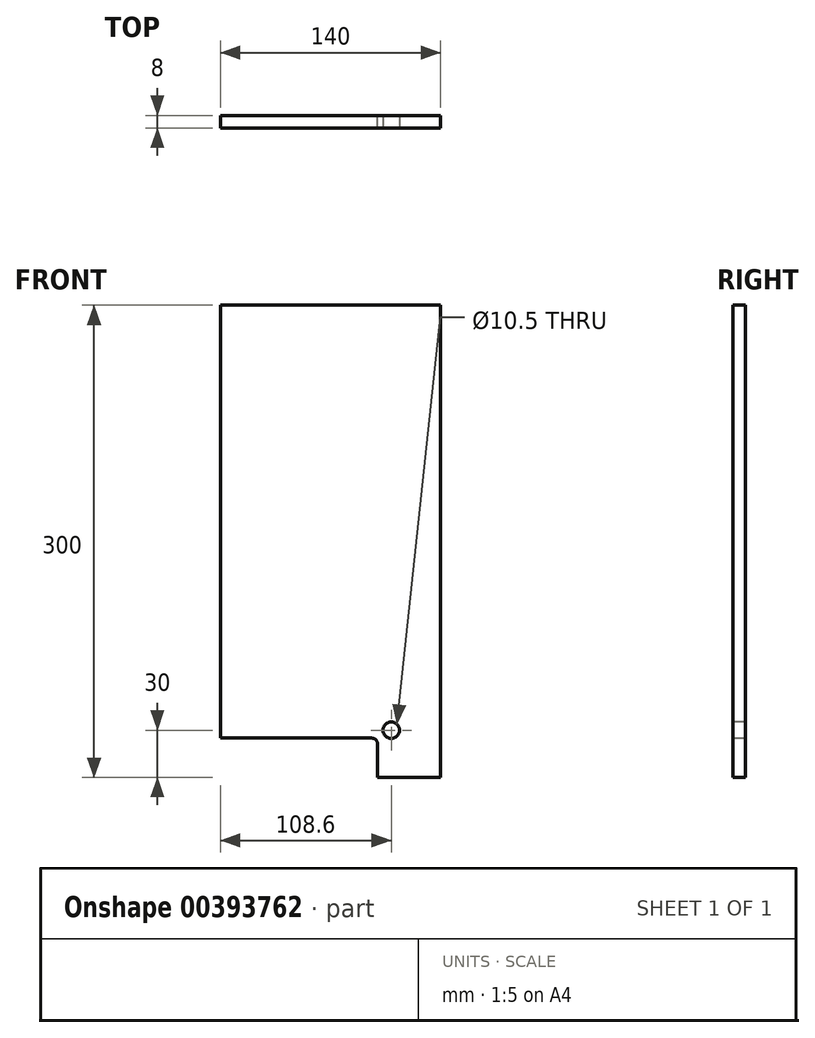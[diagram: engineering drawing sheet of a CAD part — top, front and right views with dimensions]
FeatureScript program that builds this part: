
annotation { "Feature Type Name" : "Feature", "Feature Type Description" : "" }
export const myFeature = defineFeature(function(context is Context, id is Id, definition is map)
    precondition{}
    {
        {
            var Q0;
            Q0=qCreatedBy(makeId("Front.planeOp"),FACE);
            var sketch = newSketch(context, id + "F0", { "sketchPlane" : qUnion([Q0])});
            skLineSegment(sketch, "E0", {"start": v(0, 0) * mm, "end": v(140, 0) * mm});
            skLineSegment(sketch, "E1", {"start": v(140, 0) * mm, "end": v(140, -300) * mm});
            skLineSegment(sketch, "E2", {"start": v(140, -300) * mm, "end": v(100, -300) * mm});
            skLineSegment(sketch, "E3", {"start": v(100, -300) * mm, "end": v(100, -275) * mm});
            skLineSegment(sketch, "E4", {"start": v(100, -275) * mm, "end": v(0, -275) * mm});
            skLineSegment(sketch, "E5", {"start": v(0, -275) * mm, "end": v(0, 0) * mm});
            skSolve(sketch);
        }
        {
            var Q0;
            Q0=makeQuery(id+"F0.imprint","IMPRINT",FACE,{"disambiguationData":[TD([[makeQuery(id+"F0.imprint","IMPRINT",EDGE,{"derivedFrom":sQuery(id+"F0.wireOp",EDGE,"E0")}),-1.0]])]});
            extrude(context, id + "F1", {"entities" : qUnion([Q0]), "depth" : 8 * mm});
        }
        {
            var Q0;
            Q0=makeQuery(id+"F1.opExtrude","SWEPT_EDGE",EDGE,{"disambiguationData":[OSD([sQuery(id+"F0.wireOp",EDGE,"E3"),sQuery(id+"F0.wireOp",EDGE,"E4")])]});
            fillet(context, id + "F2", {"entities" : qUnion([Q0]), "radius" : 4 * mm, "tangentPropagation" : true, "allowEdgeOverflow" : false});
        }
        {
            var Q0;
            Q0=makeQuery(id+"F1.opExtrude","CAP_FACE",FACE,{"disambiguationData":[OSD([sQuery(id+"F0.wireOp",EDGE,"E0"),sQuery(id+"F0.wireOp",EDGE,"E1"),sQuery(id+"F0.wireOp",EDGE,"E2"),sQuery(id+"F0.wireOp",EDGE,"E3"),sQuery(id+"F0.wireOp",EDGE,"E4"),sQuery(id+"F0.wireOp",EDGE,"E5")])],"isStart":false});
            var sketch = newSketch(context, id + "F3", { "sketchPlane" : qUnion([Q0])});
            skPoint(sketch, "E6", {"position": v(108.6, -270) * mm});
            skSolve(sketch);
        }
        {
            var Q0;
            Q0=sQuery(id+"F3.wireOp",VERTEX,"E6");
            var Q1;
            Q1=makeQuery(id+"F1.opExtrude","SWEPT_BODY",BODY,{"disambiguationData":[OSD([sQuery(id+"F0.wireOp",EDGE,"E0"),sQuery(id+"F0.wireOp",EDGE,"E1"),sQuery(id+"F0.wireOp",EDGE,"E2"),sQuery(id+"F0.wireOp",EDGE,"E3"),sQuery(id+"F0.wireOp",EDGE,"E4"),sQuery(id+"F0.wireOp",EDGE,"E5")])]});
            hole(context, id + "F4", {"style" : HoleStyle.SIMPLE, "endStyle" : HoleEndStyle.THROUGH, "holeDiameter" : 10.5 * mm, "isTappedThrough" : true, "tappedDepth" : 12 * mm, "tapClearance" : 3, "locations" : qUnion([Q0]), "scope" : qUnion([Q1])});
        }
    });
